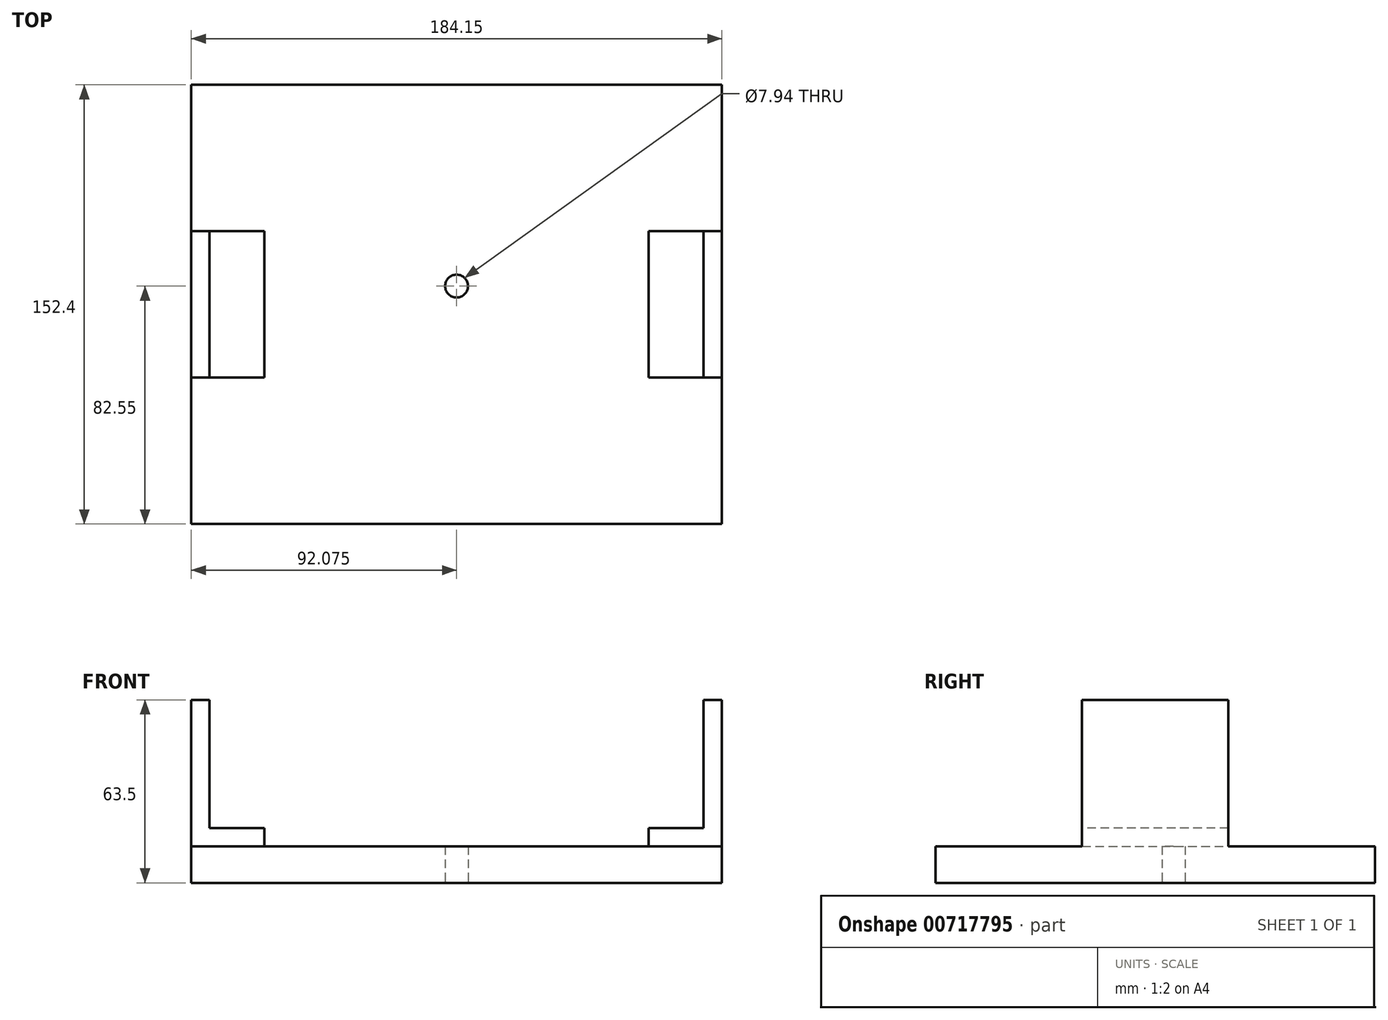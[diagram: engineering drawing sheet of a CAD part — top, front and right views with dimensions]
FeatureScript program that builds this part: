
annotation { "Feature Type Name" : "Feature", "Feature Type Description" : "" }
export const myFeature = defineFeature(function(context is Context, id is Id, definition is map)
    precondition{}
    {
        {
            var Q0;
            Q0=qCreatedBy(makeId("Top.planeOp"),FACE);
            var sketch = newSketch(context, id + "F0", { "sketchPlane" : qUnion([Q0])});
            skLineSegment(sketch, "E0.bottom", {"start": v(0, 0) * mm, "end": v(184.15, 0) * mm});
            skLineSegment(sketch, "E0.top", {"start": v(0, 152.4) * mm, "end": v(184.15, 152.4) * mm});
            skLineSegment(sketch, "E0.left", {"start": v(0, 0) * mm, "end": v(0, 152.4) * mm});
            skLineSegment(sketch, "E0.right", {"start": v(184.15, 0) * mm, "end": v(184.15, 152.4) * mm});
            skSolve(sketch);
        }
        {
            var Q0;
            Q0 = qSketchRegion(id + "F0", true);
            extrude(context, id + "F1", {"entities" : qUnion([Q0]), "depth" : 12.7 * mm, "offsetDistance" : 25.4 * mm});
        }
        {
            var Q0;
            Q0=makeQuery(id+"F1.opExtrude","CAP_FACE",FACE,{"disambiguationData":[OSD([sQuery(id+"F0.wireOp",EDGE,"E0.bottom"),sQuery(id+"F0.wireOp",EDGE,"E0.top"),sQuery(id+"F0.wireOp",EDGE,"E0.left"),sQuery(id+"F0.wireOp",EDGE,"E0.right")])],"isStart":false});
            var sketch = newSketch(context, id + "F2", { "sketchPlane" : qUnion([Q0])});
            skSolve(sketch);
        }
        {
            var Q0;
            Q0=makeQuery(id+"F1.opExtrude","CAP_FACE",FACE,{"disambiguationData":[OSD([sQuery(id+"F0.wireOp",EDGE,"E0.bottom"),sQuery(id+"F0.wireOp",EDGE,"E0.top"),sQuery(id+"F0.wireOp",EDGE,"E0.left"),sQuery(id+"F0.wireOp",EDGE,"E0.right")])],"isStart":true});
            var sketch = newSketch(context, id + "F3", { "sketchPlane" : qUnion([Q0])});
            skCircle(sketch, "E1", {"center": v(92.08, -82.55) * mm, "radius": 3.97 * mm});
            skSolve(sketch);
        }
        {
            var Q0;
            Q0 = qSketchRegion(id + "F3", true);
            extrude(context, id + "F4", {"entities" : qUnion([Q0]), "operationType" : NewBodyOperationType.REMOVE, "oppositeDirection" : true, "depth" : 25.4 * mm, "offsetDistance" : 25.4 * mm});
        }
        {
            var Q0;
            Q0=makeQuery(id+"F2.imprint","IMPRINT",FACE,{"disambiguationData":[TD([[makeQuery(id+"F2.imprint","IMPRINT",EDGE,{"derivedFrom":makeQuery(id+"F1.opExtrude","CAP_EDGE",EDGE,{"disambiguationData":[OSD([sQuery(id+"F0.wireOp",EDGE,"E0.bottom")])],"isStart":false})}),1.0]])]});
            var sketch = newSketch(context, id + "F5", { "sketchPlane" : qUnion([Q0])});
            skLineSegment(sketch, "E2.bottom", {"start": v(0, 101.6) * mm, "end": v(25.4, 101.6) * mm});
            skLineSegment(sketch, "E2.top", {"start": v(0, 50.8) * mm, "end": v(25.4, 50.8) * mm});
            skLineSegment(sketch, "E2.left", {"start": v(0, 101.6) * mm, "end": v(0, 50.8) * mm});
            skLineSegment(sketch, "E2.right", {"start": v(25.4, 101.6) * mm, "end": v(25.4, 50.8) * mm});
            skLineSegment(sketch, "E3.bottom", {"start": v(184.15, 50.8) * mm, "end": v(158.75, 50.8) * mm});
            skLineSegment(sketch, "E3.top", {"start": v(184.15, 101.6) * mm, "end": v(158.75, 101.6) * mm});
            skLineSegment(sketch, "E3.left", {"start": v(184.15, 50.8) * mm, "end": v(184.15, 101.6) * mm});
            skLineSegment(sketch, "E3.right", {"start": v(158.75, 50.8) * mm, "end": v(158.75, 101.6) * mm});
            skSolve(sketch);
        }
        {
            var Q0;
            Q0 = qSketchRegion(id + "F5", true);
            extrude(context, id + "F6", {"entities" : qUnion([Q0]), "operationType" : NewBodyOperationType.ADD, "depth" : 6.35 * mm, "offsetDistance" : 25.4 * mm});
        }
        {
            var Q0;
            Q0=makeQuery(id+"F6.opExtrude","CAP_FACE",FACE,{"disambiguationData":[OSD([sQuery(id+"F5.wireOp",EDGE,"E2.bottom"),sQuery(id+"F5.wireOp",EDGE,"E2.top"),sQuery(id+"F5.wireOp",EDGE,"E2.left"),sQuery(id+"F5.wireOp",EDGE,"E2.right")])],"isStart":false});
            var sketch = newSketch(context, id + "F7", { "sketchPlane" : qUnion([Q0])});
            skLineSegment(sketch, "E4", {"start": v(0, 101.6) * mm, "end": v(6.35, 101.6) * mm});
            skLineSegment(sketch, "E5", {"start": v(6.35, 101.6) * mm, "end": v(6.35, 50.8) * mm});
            skLineSegment(sketch, "E6", {"start": v(6.35, 50.8) * mm, "end": v(0, 50.8) * mm});
            skLineSegment(sketch, "E7", {"start": v(0, 50.8) * mm, "end": v(0, 101.6) * mm});
            skSolve(sketch);
        }
        {
            var Q0;
            Q0 = qSketchRegion(id + "F7", true);
            extrude(context, id + "F8", {"entities" : qUnion([Q0]), "operationType" : NewBodyOperationType.ADD, "depth" : 44.45 * mm, "offsetDistance" : 25.4 * mm});
        }
        {
            var Q0;
            Q0=makeQuery(id+"F6.opExtrude","CAP_FACE",FACE,{"disambiguationData":[OSD([sQuery(id+"F5.wireOp",EDGE,"E3.bottom"),sQuery(id+"F5.wireOp",EDGE,"E3.top"),sQuery(id+"F5.wireOp",EDGE,"E3.left"),sQuery(id+"F5.wireOp",EDGE,"E3.right")])],"isStart":false});
            var sketch = newSketch(context, id + "F9", { "sketchPlane" : qUnion([Q0])});
            skLineSegment(sketch, "E8.bottom", {"start": v(184.15, 101.6) * mm, "end": v(177.8, 101.6) * mm});
            skLineSegment(sketch, "E8.top", {"start": v(184.15, 50.8) * mm, "end": v(177.8, 50.8) * mm});
            skLineSegment(sketch, "E8.left", {"start": v(184.15, 101.6) * mm, "end": v(184.15, 50.8) * mm});
            skLineSegment(sketch, "E8.right", {"start": v(177.8, 101.6) * mm, "end": v(177.8, 50.8) * mm});
            skSolve(sketch);
        }
        {
            var Q0;
            Q0 = qSketchRegion(id + "F9", true);
            extrude(context, id + "F10", {"entities" : qUnion([Q0]), "operationType" : NewBodyOperationType.ADD, "depth" : 44.45 * mm, "offsetDistance" : 25.4 * mm});
        }
    });
